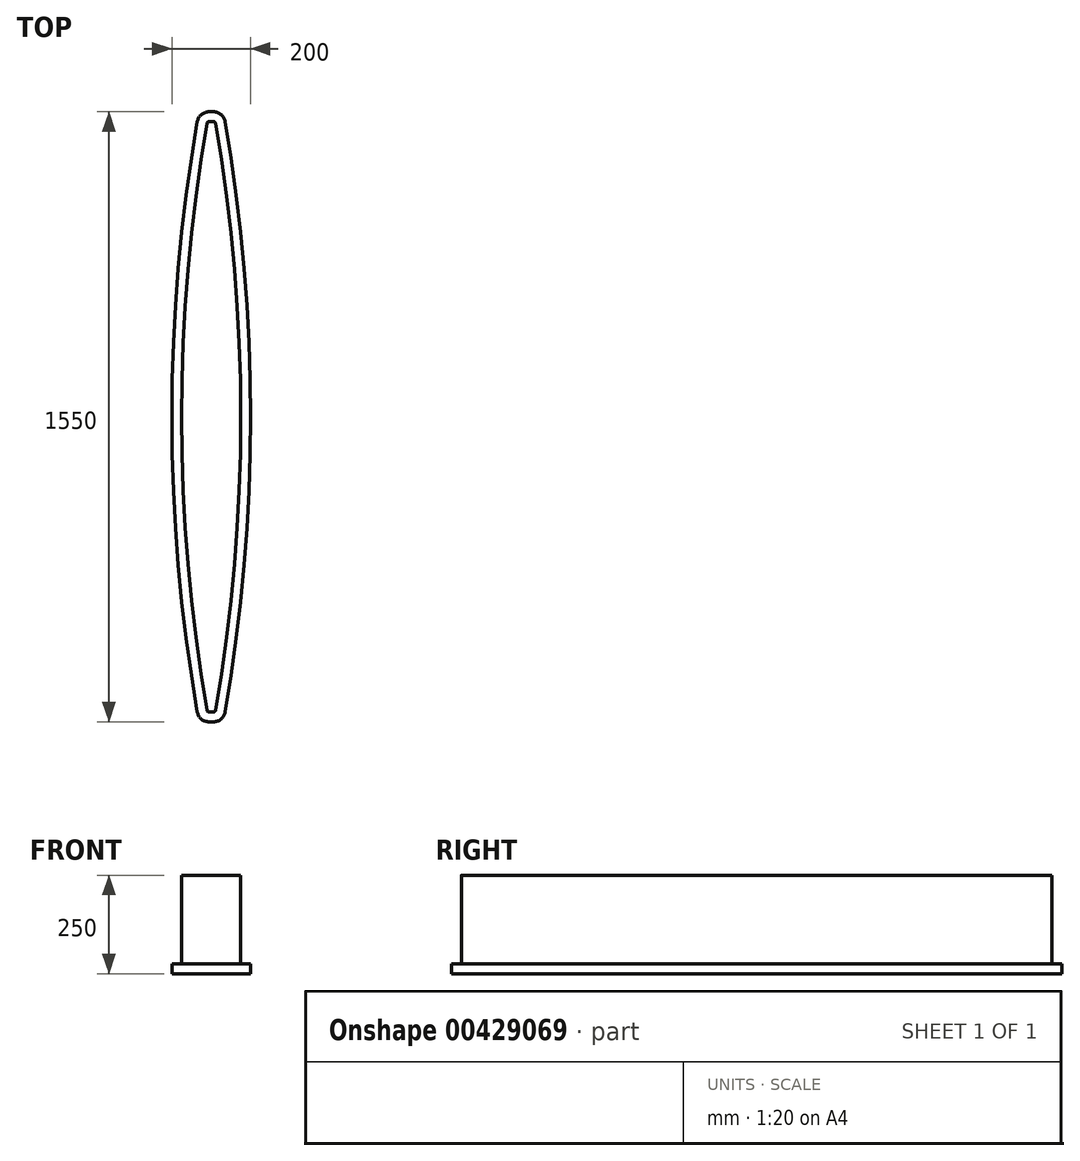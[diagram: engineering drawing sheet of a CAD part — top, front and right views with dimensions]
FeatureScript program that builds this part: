
annotation { "Feature Type Name" : "Feature", "Feature Type Description" : "" }
export const myFeature = defineFeature(function(context is Context, id is Id, definition is map)
    precondition{}
    {
        {
            var Q0;
            Q0=qCreatedBy(makeId("Top.planeOp"),FACE);
            var sketch = newSketch(context, id + "F0", { "sketchPlane" : qUnion([Q0])});
            skLineSegment(sketch, "E0", {"start": v(0, 0) * mm, "end": v(0, 750) * mm});
            skLineSegment(sketch, "E1", {"start": v(0, 750) * mm, "end": v(-10, 750) * mm});
            skLineSegment(sketch, "E2", {"start": v(0, 0) * mm, "end": v(-75, 0) * mm});
            skLineSegment(sketch, "E3", {"start": v(-75, 0) * mm, "end": v(-75, -273.78) * mm, "construction": true});
            skArc(sketch, "E4", {"start": v(-75, 0) * mm, "mid": v(-58.72, 376.4) * mm, "end": v(-10, 750) * mm});
            skSolve(sketch);
        }
        {
            var Q0;
            Q0=makeQuery(id+"F0.imprint","IMPRINT",FACE,{"disambiguationData":[TD([[makeQuery(id+"F0.imprint","IMPRINT",EDGE,{"derivedFrom":sQuery(id+"F0.wireOp",EDGE,"E0")}),1.0]])]});
            extrude(context, id + "F1", {"entities" : qUnion([Q0]), "depth" : 250 * mm});
        }
        {
            var Q0;
            Q0=makeQuery(id+"F1.opExtrude","SWEPT_BODY",BODY,{"disambiguationData":[OSD([sQuery(id+"F0.wireOp",EDGE,"E0"),sQuery(id+"F0.wireOp",EDGE,"E1"),sQuery(id+"F0.wireOp",EDGE,"E2"),sQuery(id+"F0.wireOp",EDGE,"E4")])]});
            var Q1;
            Q1=makeQuery(id+"F1.opExtrude","SWEPT_FACE",FACE,{"disambiguationData":[OSD([sQuery(id+"F0.wireOp",EDGE,"E2")])]});
            mirror(context, id + "F2", {"operationType" : NewBodyOperationType.ADD, "entities" : qUnion([Q0]), "mirrorPlane" : qUnion([Q1])});
        }
        {
            var Q0;
            Q0=makeQuery(id+"F1.opExtrude","SWEPT_BODY",BODY,{"disambiguationData":[OSD([sQuery(id+"F0.wireOp",EDGE,"E0"),sQuery(id+"F0.wireOp",EDGE,"E1"),sQuery(id+"F0.wireOp",EDGE,"E2"),sQuery(id+"F0.wireOp",EDGE,"E4")])]});
            var Q1;
            {var subQ0=makeQuery(id+"F1.opExtrude","SWEPT_FACE",FACE,{"disambiguationData":[OSD([sQuery(id+"F0.wireOp",EDGE,"E0")])]});Q1=makeQuery(id+"F2.boolean.opBoolean","MERGE",FACE,{"derivedFrom":[subQ0,makeQuery(id+"F2.opPattern","COPY",FACE,{"derivedFrom":subQ0,"instanceName":"1"})]});}
            mirror(context, id + "F3", {"operationType" : NewBodyOperationType.ADD, "entities" : qUnion([Q0]), "mirrorPlane" : qUnion([Q1])});
        }
        {
            var Q0;
            Q0=makeQuery(id+"F2.opPattern","COPY",EDGE,{"derivedFrom":makeQuery(id+"F1.opExtrude","SWEPT_EDGE",EDGE,{"disambiguationData":[OSD([sQuery(id+"F0.wireOp",EDGE,"E1"),sQuery(id+"F0.wireOp",EDGE,"E4")])]}),"instanceName":"1"});
            var Q1;
            Q1=makeQuery(id+"F3.opPattern","COPY",EDGE,{"derivedFrom":makeQuery(id+"F2.opPattern","COPY",EDGE,{"derivedFrom":makeQuery(id+"F1.opExtrude","SWEPT_EDGE",EDGE,{"disambiguationData":[OSD([sQuery(id+"F0.wireOp",EDGE,"E1"),sQuery(id+"F0.wireOp",EDGE,"E4")])]}),"instanceName":"1"}),"instanceName":"1"});
            var Q2;
            Q2=makeQuery(id+"F3.opPattern","COPY",EDGE,{"derivedFrom":makeQuery(id+"F1.opExtrude","SWEPT_EDGE",EDGE,{"disambiguationData":[OSD([sQuery(id+"F0.wireOp",EDGE,"E1"),sQuery(id+"F0.wireOp",EDGE,"E4")])]}),"instanceName":"1"});
            var Q3;
            Q3=makeQuery(id+"F1.opExtrude","SWEPT_EDGE",EDGE,{"disambiguationData":[OSD([sQuery(id+"F0.wireOp",EDGE,"E1"),sQuery(id+"F0.wireOp",EDGE,"E4")])]});
            fillet(context, id + "F4", {"entities" : qUnion([Q0, Q1, Q2, Q3]), "radius" : 5 * mm, "tangentPropagation" : true, "allowEdgeOverflow" : false});
        }
        {
            var Q0;
            {var subQ0=makeQuery(id+"F1.opExtrude","CAP_FACE",FACE,{"disambiguationData":[OSD([sQuery(id+"F0.wireOp",EDGE,"E0"),sQuery(id+"F0.wireOp",EDGE,"E1"),sQuery(id+"F0.wireOp",EDGE,"E2"),sQuery(id+"F0.wireOp",EDGE,"E4")])],"isStart":true});var subQ1=makeQuery(id+"F2.boolean.opBoolean","MERGE",FACE,{"derivedFrom":[subQ0,makeQuery(id+"F2.opPattern","COPY",FACE,{"derivedFrom":subQ0,"instanceName":"1"})]});Q0=makeQuery(id+"F3.boolean.opBoolean","MERGE",FACE,{"derivedFrom":[subQ1,makeQuery(id+"F3.opPattern","COPY",FACE,{"derivedFrom":subQ1,"instanceName":"1"})]});}
            var sketch = newSketch(context, id + "F5", { "sketchPlane" : qUnion([Q0])});
            skArc(sketch, "E5.0", {"start": v(35.35, 750.13) * mm, "mid": v(100, 0) * mm, "end": v(35.35, -750.13) * mm});
            skArc(sketch, "E6.0", {"start": v(-35.35, 750.13) * mm, "mid": v(-100, 0) * mm, "end": v(-35.35, -750.13) * mm});
            skLineSegment(sketch, "E7.0", {"start": v(5.8, 775) * mm, "end": v(-5.8, 775) * mm});
            skArc(sketch, "E8.0", {"start": v(5.8, 775) * mm, "mid": v(25.1, 767.96) * mm, "end": v(35.35, 750.13) * mm});
            skArc(sketch, "E9.0", {"start": v(-35.35, 750.13) * mm, "mid": v(-25.1, 767.96) * mm, "end": v(-5.8, 775) * mm});
            skLineSegment(sketch, "E10.0", {"start": v(5.8, -775) * mm, "end": v(-5.8, -775) * mm});
            skArc(sketch, "E11.0", {"start": v(35.35, -750.13) * mm, "mid": v(25.1, -767.96) * mm, "end": v(5.8, -775) * mm});
            skArc(sketch, "E12.0", {"start": v(-5.8, -775) * mm, "mid": v(-25.1, -767.96) * mm, "end": v(-35.35, -750.13) * mm});
            skSolve(sketch);
        }
        {
            var Q0;
            Q0 = qSketchRegion(id + "F5", true);
            extrude(context, id + "F6", {"entities" : qUnion([Q0]), "operationType" : NewBodyOperationType.ADD, "oppositeDirection" : true, "depth" : 25 * mm});
        }
    });
